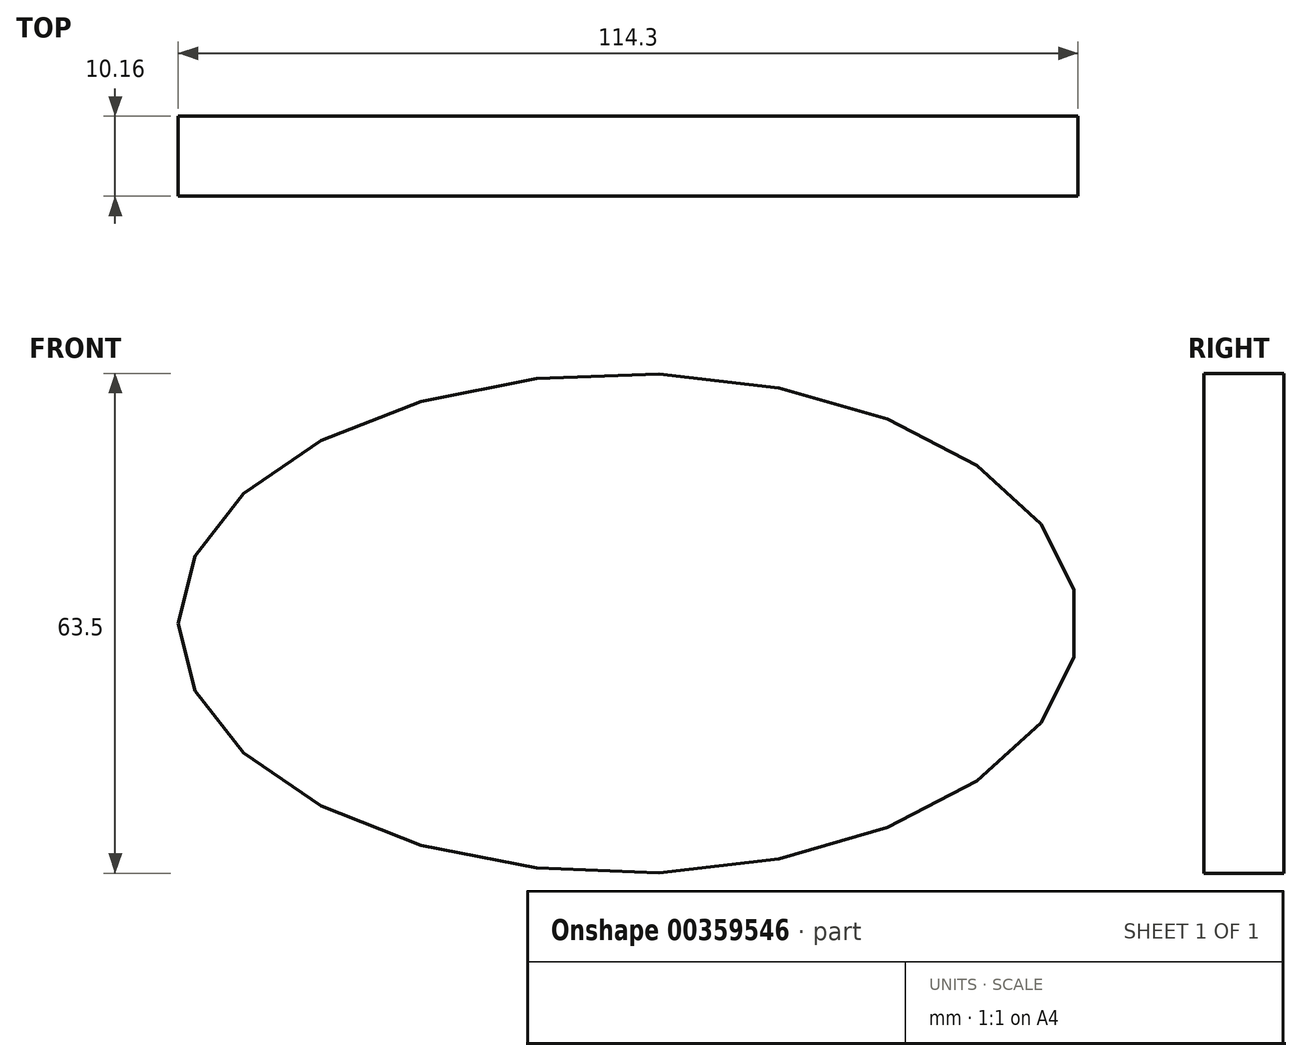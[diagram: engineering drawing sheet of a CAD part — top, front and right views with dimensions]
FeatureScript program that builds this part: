
annotation { "Feature Type Name" : "Feature", "Feature Type Description" : "" }
export const myFeature = defineFeature(function(context is Context, id is Id, definition is map)
    precondition{}
    {
        {
            var Q0;
            Q0=qCreatedBy(makeId("Front.planeOp"),FACE);
            var sketch = newSketch(context, id + "F0", { "sketchPlane" : qUnion([Q0])});
            skEllipse(sketch, "E0", {"center": v(0, 0) * mm, "majorRadius": 57.15 * mm, "minorRadius": 31.75 * mm, "majorAxis": v(-1, 0)});
            skPoint(sketch, "E1", {"position": v(-57.15, 0) * mm});
            skPoint(sketch, "E2", {"position": v(0, 31.75) * mm});
            skPoint(sketch, "E3", {"position": v(0, -31.75) * mm});
            skPoint(sketch, "E4", {"position": v(57.15, 0) * mm});
            skSolve(sketch);
        }
        {
            var Q0;
            Q0=makeQuery(id+"F0.imprint","IMPRINT",FACE,{"disambiguationData":[TD([[makeQuery(id+"F0.imprint","IMPRINT",EDGE,{"derivedFrom":sQuery(id+"F0.wireOp",EDGE,"E0")}),1.0]])]});
            extrude(context, id + "F1", {"entities" : qUnion([Q0]), "depth" : 10.16 * mm});
        }
    });
